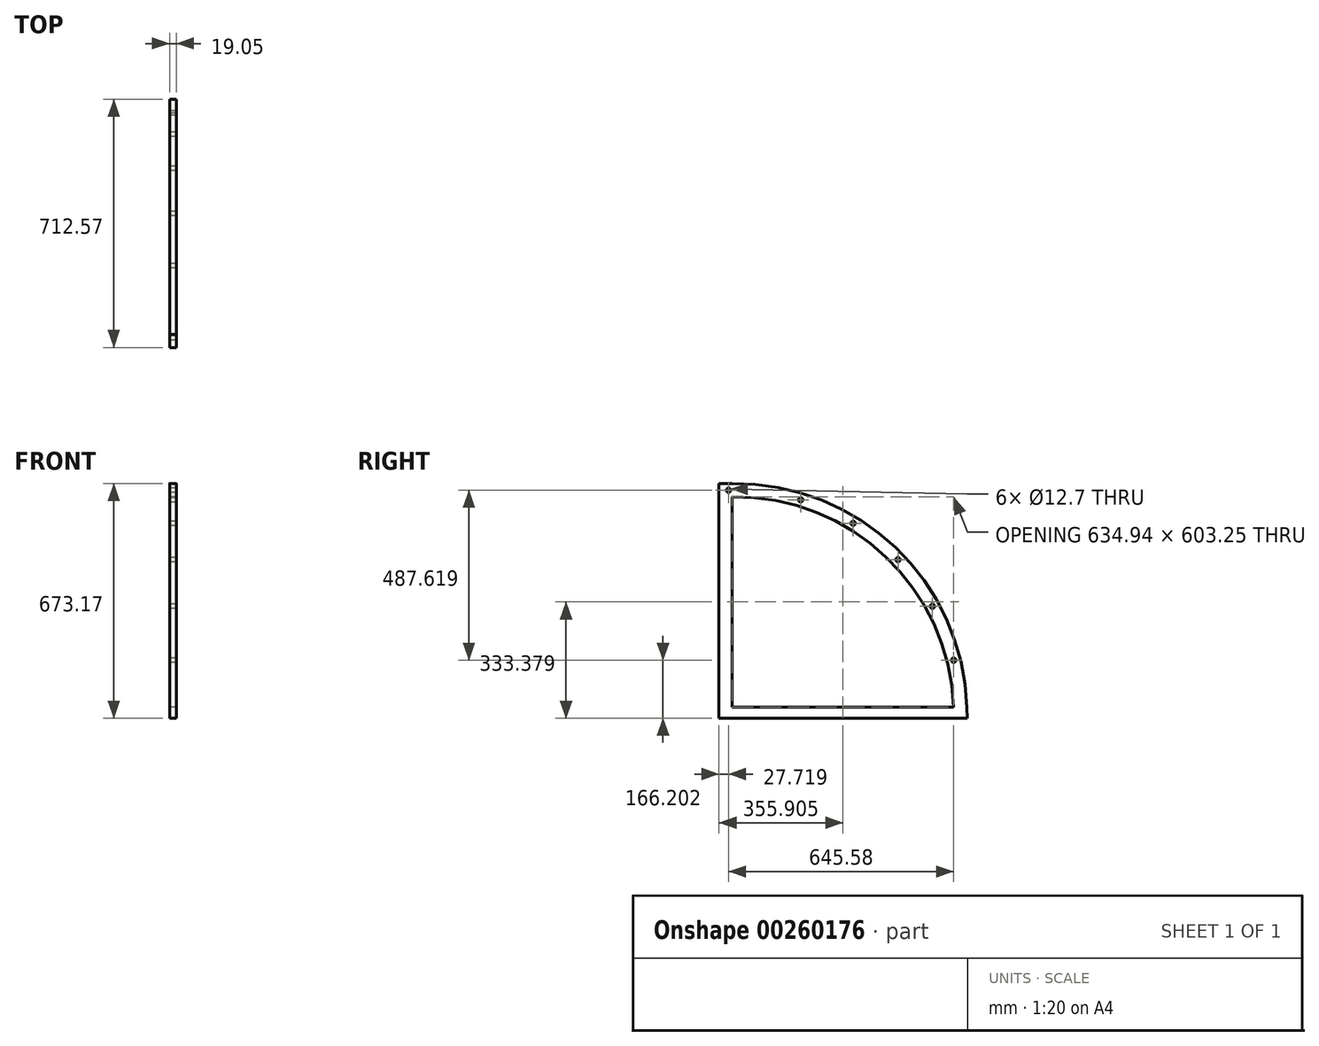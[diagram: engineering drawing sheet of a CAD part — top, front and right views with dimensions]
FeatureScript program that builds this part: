
annotation { "Feature Type Name" : "Feature", "Feature Type Description" : "" }
export const myFeature = defineFeature(function(context is Context, id is Id, definition is map)
    precondition{}
    {
        {
            var Q0;
            Q0=qCreatedBy(makeId("Right.planeOp"),FACE);
            var sketch = newSketch(context, id + "F0", { "sketchPlane" : qUnion([Q0])});
            skLineSegment(sketch, "E0", {"start": v(295.62, -164.98) * mm, "end": v(-339.33, -164.98) * mm});
            skLineSegment(sketch, "E1", {"start": v(-339.33, -164.98) * mm, "end": v(274.04, -0.63) * mm, "construction": true});
            skLineSegment(sketch, "E2", {"start": v(-339.33, -164.98) * mm, "end": v(210.6, 152.52) * mm, "construction": true});
            skLineSegment(sketch, "E3", {"start": v(-339.33, -164.98) * mm, "end": v(109.69, 284.04) * mm, "construction": true});
            skLineSegment(sketch, "E4", {"start": v(-339.33, -164.98) * mm, "end": v(-21.83, 384.95) * mm, "construction": true});
            skLineSegment(sketch, "E5", {"start": v(-339.33, -164.98) * mm, "end": v(-174.98, 448.39) * mm, "construction": true});
            skLineSegment(sketch, "E6", {"start": v(-339.33, -164.98) * mm, "end": v(-339.33, 438.27) * mm});
            skArc(sketch, "E7", {"start": v(314.68, -164.98) * mm, "mid": v(112.94, 280.98) * mm, "end": v(-343.7, 457.25) * mm, "construction": true});
            skCircle(sketch, "E8", {"center": v(-174.98, 448.39) * mm, "radius": 36.83 * mm, "construction": true});
            skCircle(sketch, "E9", {"center": v(-21.83, 384.95) * mm, "radius": 36.83 * mm, "construction": true});
            skCircle(sketch, "E10", {"center": v(109.69, 284.04) * mm, "radius": 36.83 * mm, "construction": true});
            skCircle(sketch, "E11", {"center": v(210.6, 152.52) * mm, "radius": 36.83 * mm, "construction": true});
            skCircle(sketch, "E12", {"center": v(274.04, -0.63) * mm, "radius": 36.83 * mm, "construction": true});
            skCircle(sketch, "E13", {"center": v(295.54, -30.53) * mm, "radius": 6.35 * mm});
            skLineSegment(sketch, "E14", {"start": v(293.96, -24.38) * mm, "end": v(274.04, -0.63) * mm, "construction": true});
            skCircle(sketch, "E15", {"center": v(234.36, 124.38) * mm, "radius": 6.35 * mm});
            skCircle(sketch, "E16", {"center": v(135.9, 258.17) * mm, "radius": 6.35 * mm});
            skCircle(sketch, "E17", {"center": v(7.06, 362.1) * mm, "radius": 6.35 * mm});
            skCircle(sketch, "E18", {"center": v(-143.28, 429.64) * mm, "radius": 6.35 * mm});
            skArc(sketch, "E19.0", {"start": v(333.77, -165.93) * mm, "mid": v(128.22, 292.74) * mm, "end": v(-339.66, 476.37) * mm});
            skArc(sketch, "E20.0", {"start": v(295.62, -164.98) * mm, "mid": v(101.05, 266) * mm, "end": v(-339.33, 438.27) * mm});
            skCircle(sketch, "E21", {"center": v(-350.04, 457.1) * mm, "radius": 6.35 * mm});
            skLineSegment(sketch, "E22", {"start": v(-339.66, 476.37) * mm, "end": v(-377.76, 476.37) * mm});
            skLineSegment(sketch, "E23", {"start": v(-377.76, 476.37) * mm, "end": v(-377.76, -196.73) * mm});
            skLineSegment(sketch, "E24.0", {"start": v(-377.76, -196.73) * mm, "end": v(314.39, -196.73) * mm});
            skPoint(sketch, "E25.end.orphan", {"position": v(314.72, -196.73) * mm});
            skLineSegment(sketch, "E26", {"start": v(333.77, -165.93) * mm, "end": v(334.8, -196.73) * mm});
            skLineSegment(sketch, "E27", {"start": v(314.39, -196.73) * mm, "end": v(334.8, -196.73) * mm});
            skSolve(sketch);
        }
        {
            var Q0;
            Q0 = qSketchRegion(id + "F0", true);
            extrude(context, id + "F1", {"entities" : qUnion([Q0]), "depth" : 19.05 * mm});
        }
    });
